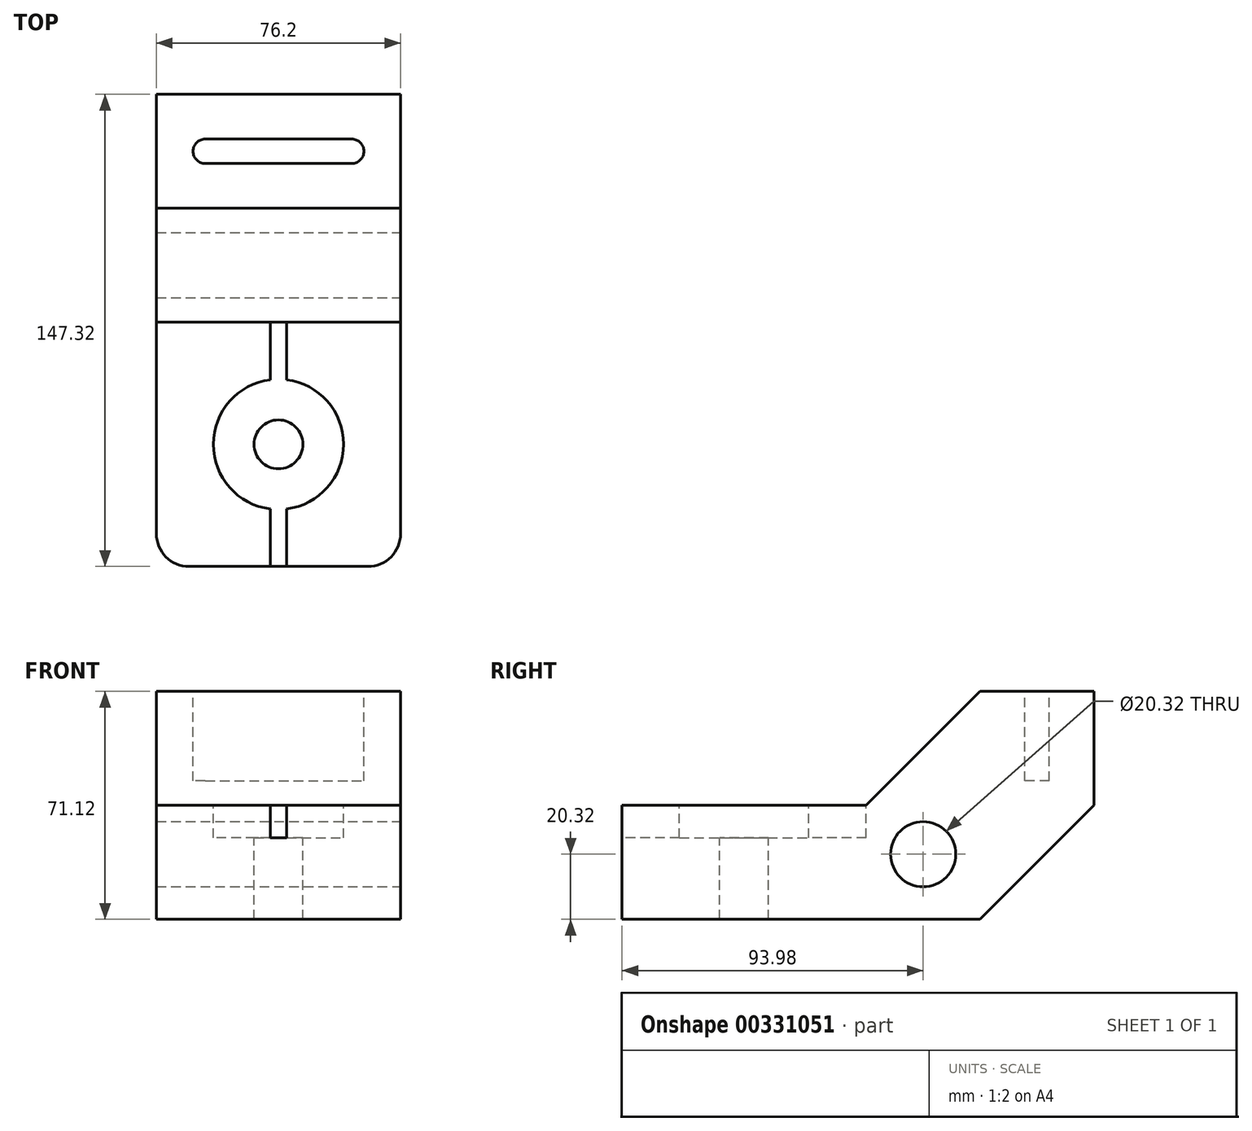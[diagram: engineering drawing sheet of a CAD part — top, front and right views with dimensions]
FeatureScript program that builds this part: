
annotation { "Feature Type Name" : "Feature", "Feature Type Description" : "" }
export const myFeature = defineFeature(function(context is Context, id is Id, definition is map)
    precondition{}
    {
        {
            var Q0;
            Q0=qCreatedBy(makeId("Right.planeOp"),FACE);
            var sketch = newSketch(context, id + "F0", { "sketchPlane" : qUnion([Q0])});
            skLineSegment(sketch, "E0", {"start": v(0, 0) * mm, "end": v(111.76, 0) * mm});
            skLineSegment(sketch, "E1", {"start": v(111.76, 0) * mm, "end": v(147.32, 35.56) * mm});
            skLineSegment(sketch, "E2", {"start": v(147.32, 35.56) * mm, "end": v(147.32, 71.12) * mm});
            skLineSegment(sketch, "E3", {"start": v(147.32, 71.12) * mm, "end": v(111.76, 71.12) * mm});
            skLineSegment(sketch, "E4", {"start": v(111.76, 71.12) * mm, "end": v(76.2, 35.56) * mm});
            skLineSegment(sketch, "E5", {"start": v(76.2, 35.56) * mm, "end": v(0, 35.56) * mm});
            skLineSegment(sketch, "E6", {"start": v(0, 35.56) * mm, "end": v(0, 0) * mm});
            skSolve(sketch);
        }
        {
            var Q0;
            Q0 = qSketchRegion(id + "F0", true);
            extrude(context, id + "F1", {"entities" : qUnion([Q0]), "depth" : 76.2 * mm});
        }
        {
            var Q0;
            Q0=makeQuery(id+"F1.opExtrude","SWEPT_FACE",FACE,{"disambiguationData":[OSD([sQuery(id+"F0.wireOp",EDGE,"E5")])]});
            var sketch = newSketch(context, id + "F2", { "sketchPlane" : qUnion([Q0])});
            skPoint(sketch, "E7", {"position": v(38.1, 38.1) * mm});
            skSolve(sketch);
        }
        {
            var Q0;
            Q0=sQuery(id+"F2.wireOp",VERTEX,"E7");
            var Q1;
            Q1=makeQuery(id+"F1.opExtrude","SWEPT_BODY",BODY,{"disambiguationData":[OSD([sQuery(id+"F0.wireOp",EDGE,"E0"),sQuery(id+"F0.wireOp",EDGE,"E1"),sQuery(id+"F0.wireOp",EDGE,"E2"),sQuery(id+"F0.wireOp",EDGE,"E3"),sQuery(id+"F0.wireOp",EDGE,"E4"),sQuery(id+"F0.wireOp",EDGE,"E5"),sQuery(id+"F0.wireOp",EDGE,"E6")])]});
            hole(context, id + "F3", {"style" : HoleStyle.C_BORE, "endStyle" : HoleEndStyle.THROUGH, "holeDiameter" : 15.24 * mm, "cBoreDiameter" : 40.64 * mm, "cBoreDepth" : 10.16 * mm, "tappedDepth" : 12.7 * mm, "tapClearance" : 3, "locations" : qUnion([Q0]), "scope" : qUnion([Q1])});
        }
        {
            var Q0;
            Q0=makeQuery(id+"F1.opExtrude","SWEPT_FACE",FACE,{"disambiguationData":[OSD([sQuery(id+"F0.wireOp",EDGE,"E6")])]});
            var sketch = newSketch(context, id + "F4", { "sketchPlane" : qUnion([Q0])});
            skLineSegment(sketch, "E8", {"start": v(38.1, 35.56) * mm, "end": v(35.56, 35.56) * mm});
            skLineSegment(sketch, "E9", {"start": v(38.1, 35.56) * mm, "end": v(40.64, 35.56) * mm});
            skLineSegment(sketch, "E10", {"start": v(40.64, 35.56) * mm, "end": v(40.64, 25.4) * mm});
            skLineSegment(sketch, "E11", {"start": v(40.64, 25.4) * mm, "end": v(35.56, 25.4) * mm});
            skLineSegment(sketch, "E12", {"start": v(35.56, 25.4) * mm, "end": v(35.56, 35.56) * mm});
            skSolve(sketch);
        }
        {
            var Q0;
            Q0 = qSketchRegion(id + "F4", true);
            extrude(context, id + "F5", {"entities" : qUnion([Q0]), "operationType" : NewBodyOperationType.REMOVE, "oppositeDirection" : true, "depth" : 76.2 * mm});
        }
        {
            var Q0;
            Q0=makeQuery(id+"F1.opExtrude","CAP_FACE",FACE,{"disambiguationData":[OSD([sQuery(id+"F0.wireOp",EDGE,"E0"),sQuery(id+"F0.wireOp",EDGE,"E1"),sQuery(id+"F0.wireOp",EDGE,"E2"),sQuery(id+"F0.wireOp",EDGE,"E3"),sQuery(id+"F0.wireOp",EDGE,"E4"),sQuery(id+"F0.wireOp",EDGE,"E5"),sQuery(id+"F0.wireOp",EDGE,"E6")])],"isStart":false});
            var sketch = newSketch(context, id + "F6", { "sketchPlane" : qUnion([Q0])});
            skCircle(sketch, "E13", {"center": v(93.98, 20.32) * mm, "radius": 10.16 * mm});
            skSolve(sketch);
        }
        {
            var Q0;
            Q0 = qSketchRegion(id + "F6", true);
            extrude(context, id + "F7", {"entities" : qUnion([Q0]), "operationType" : NewBodyOperationType.REMOVE, "oppositeDirection" : true, "depth" : 76.2 * mm});
        }
        {
            var Q0;
            Q0=makeQuery(id+"F1.opExtrude","SWEPT_FACE",FACE,{"disambiguationData":[OSD([sQuery(id+"F0.wireOp",EDGE,"E3")])]});
            var sketch = newSketch(context, id + "F8", { "sketchPlane" : qUnion([Q0])});
            skArc(sketch, "E14", {"start": v(15.24, 133.35) * mm, "mid": v(11.43, 129.54) * mm, "end": v(15.24, 125.73) * mm});
            skArc(sketch, "E15", {"start": v(60.96, 125.73) * mm, "mid": v(64.77, 129.54) * mm, "end": v(60.96, 133.35) * mm});
            skLineSegment(sketch, "E16", {"start": v(15.24, 133.35) * mm, "end": v(60.96, 133.35) * mm});
            skLineSegment(sketch, "E17", {"start": v(15.24, 125.73) * mm, "end": v(60.96, 125.73) * mm});
            skSolve(sketch);
        }
        {
            var Q0;
            Q0 = qSketchRegion(id + "F8", true);
            extrude(context, id + "F9", {"entities" : qUnion([Q0]), "operationType" : NewBodyOperationType.REMOVE, "oppositeDirection" : true, "depth" : 27.94 * mm});
        }
        {
            var Q0;
            Q0=makeQuery(id+"F1.opExtrude","CAP_EDGE",EDGE,{"disambiguationData":[OSD([sQuery(id+"F0.wireOp",EDGE,"E6")])],"isStart":true});
            var Q1;
            Q1=makeQuery(id+"F1.opExtrude","CAP_EDGE",EDGE,{"disambiguationData":[OSD([sQuery(id+"F0.wireOp",EDGE,"E6")])],"isStart":false});
            fillet(context, id + "F10", {"entities" : qUnion([Q0, Q1]), "radius" : 10.16 * mm, "tangentPropagation" : true, "allowEdgeOverflow" : false});
        }
    });
